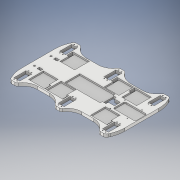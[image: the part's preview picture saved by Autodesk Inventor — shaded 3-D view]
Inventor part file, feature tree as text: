
AUTODESK INVENTOR PART (.ipt)
format: ipt  version: 2017 (Build 210142000, 142)  size: 566,784 bytes
history: native  units: mm
features: extrude x13, sketch x13, fillet x4
ambient origin geometry x8: Origin, YZ Plane, XZ Plane, XY Plane, X Axis, Y Axis, Z Axis, Center Point
bodies: Solid1 (feature_tree)
feature tree (30):
  extrude  "Extrusion1"  Depth=82.5mm
  extrude  "Extrusion2"  Depth=10.0mm
  extrude  "Extrusion3"  Depth=10.0mm
  extrude  "Extrusion4"  Depth=11.5mm
  fillet  "Fillet1"  Radius=5.0mm
  fillet  "Fillet2"  Radius=20.0mm
  extrude  "Extrusion6"  Depth=5.0mm
  extrude  "Extrusion5"  Depth=5.0mm
  extrude  "Extrusion8"  Depth=4.0mm
  fillet  "Fillet3"  Radius=4.0mm
  extrude  "Extrusion10"  Depth=4.5mm
  extrude  "Extrusion11"  Depth=5.0mm
  fillet  "Fillet4"  Radius=5.0mm
  extrude  "Extrusion12"  Depth=6.5mm
  extrude  "Extrusion13"  Depth=2.0mm
  extrude  "Extrusion15"  Depth=10.0mm
  extrude  "Extrusion17"  Depth=2.5mm
  sketch  "Sketch1"  dims[d0=30.0mm d1=82.5mm]
  sketch  "Sketch2"  dims[d2=26.75mm d3=10.0mm]
  sketch  "Sketch3"  dims[d4=120.0mm d5=10.0mm]
  sketch  "Sketch4"  dims[d6=0.0mm d7=11.5mm d8=5.0mm d9=20.0mm]
  sketch  "Sketch5"  dims[d10=40.5mm d11=5.0mm]
  sketch  "Sketch6"  dims[d12=5.0mm d13=5.0mm]
  sketch  "Sketch8"  dims[d14=0.0mm d17=4.0mm d18=4.0mm]
  sketch  "Sketch10"  dims[d19=4.5mm d25=2.75mm]
  sketch  "Sketch11"  dims[d26=2.75mm d27=2.75mm d28=5.0mm]
  sketch  "Sketch12"  dims[d29=0.0mm d30=6.5mm]
  sketch  "Sketch13"  dims[d31=1.2mm d32=2.0mm]
  sketch  "Sketch14"  dims[d33=0.0mm d37=10.0mm]
  sketch  "Sketch16"  dims[d38=50.0mm d40=85.0mm d41=56.0mm d42=2.75mm d43=3.5mm d44=3.5mm d45=3.5mm d46=58.0mm d47=10.0mm d48=0.0mm d49=51.0mm d50=120.0mm d51=5.0mm d52=0.0mm d58=50.0mm d59=50.0mm d61=10.0mm d62=10.0mm d63=10.0mm d64=5.0mm d65=0.0mm d67=3.0mm d68=20.0mm d69=100.0mm d70=3.0mm d71=10.0mm d78=50.0mm d79=36.0mm d80=2.5mm d81=0.0mm d82=40.0mm d83=5.0mm d84=75.0mm d85=5.0mm d86=5.0mm d87=0.0mm d88=36.0mm d89=12.0mm d90=2.0mm d91=20.0mm d92=6.0mm d93=10.0mm d94=0.0mm d95=6.0mm d97=10.0mm d98=0.0mm d99=8.0mm d100=15.0mm d103=5.0mm d104=0.0mm d109=12.0mm d110=10.0mm d111=0.0mm d112=5.0mm d113=2.5mm]
